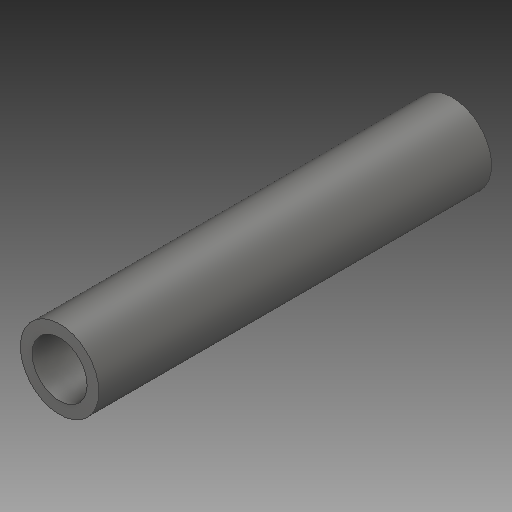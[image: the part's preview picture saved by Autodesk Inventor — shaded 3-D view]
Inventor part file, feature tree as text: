
AUTODESK INVENTOR PART (.ipt)
format: ipt  version: 2019 (Build 230136000, 136)  size: 100,864 bytes
history: native  units: in
note: dims shown in document units (in); Inventor stores cm internally (conversion verified against a paired STEP export)
features: other x3, sketch x3
ambient origin geometry x8: Origin, YZ Plane, XZ Plane, XY Plane, X Axis, Y Axis, Z Axis, Center Point
bodies: Solid1 (feature_tree)
feature tree (6):
  other  "project rolller 1 part_CPY.ipt"
  other  "Solid2::project rolller 1 part_CPY.ipt"
  other  "TaggingFeature1"
  sketch  "Sketch5"  dims[d0=0.3937in]
  sketch  "Sketch6"
  sketch  "Sketch7"
